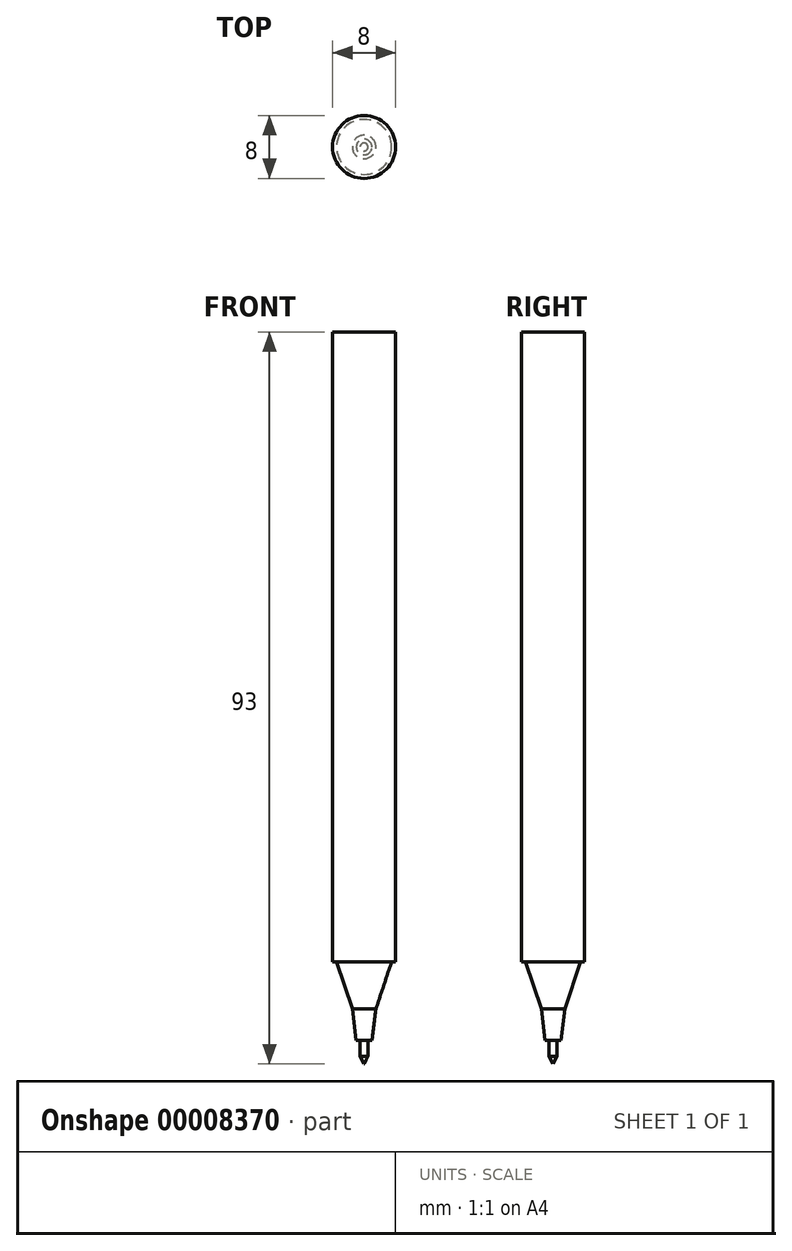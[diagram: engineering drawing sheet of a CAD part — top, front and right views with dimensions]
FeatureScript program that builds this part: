
annotation { "Feature Type Name" : "Feature", "Feature Type Description" : "" }
export const myFeature = defineFeature(function(context is Context, id is Id, definition is map)
    precondition{}
    {
        {
            var Q0;
            Q0=qCreatedBy(makeId("Front.planeOp"),FACE);
            var sketch = newSketch(context, id + "F0", { "sketchPlane" : qUnion([Q0])});
            skLineSegment(sketch, "E0", {"start": v(0, 0) * mm, "end": v(0.5, 1) * mm});
            skLineSegment(sketch, "E1", {"start": v(0.5, 1) * mm, "end": v(0.5, 3) * mm});
            skLineSegment(sketch, "E2", {"start": v(0.5, 3) * mm, "end": v(1, 3) * mm});
            skLineSegment(sketch, "E3", {"start": v(1, 3) * mm, "end": v(1.5, 7) * mm});
            skLineSegment(sketch, "E4", {"start": v(1.5, 7) * mm, "end": v(3.5, 13) * mm});
            skLineSegment(sketch, "E5", {"start": v(3.5, 13) * mm, "end": v(4, 13) * mm});
            skLineSegment(sketch, "E6", {"start": v(4, 13) * mm, "end": v(4, 93) * mm});
            skLineSegment(sketch, "E7", {"start": v(4, 93) * mm, "end": v(0, 93) * mm});
            skLineSegment(sketch, "E8", {"start": v(0, 93) * mm, "end": v(0, 0) * mm});
            skSolve(sketch);
        }
        {
            var Q0;
            Q0=qSketchRegion(id+"F0",true);
            var Q1;
            Q1=sQuery(id+"F0.wireOp",EDGE,"E8");
            revolve(context, id + "F1", {"entities" : qUnion([Q0]), "axis" : qUnion([Q1]), "revolveType" : RevolveType.FULL});
        }
    });
